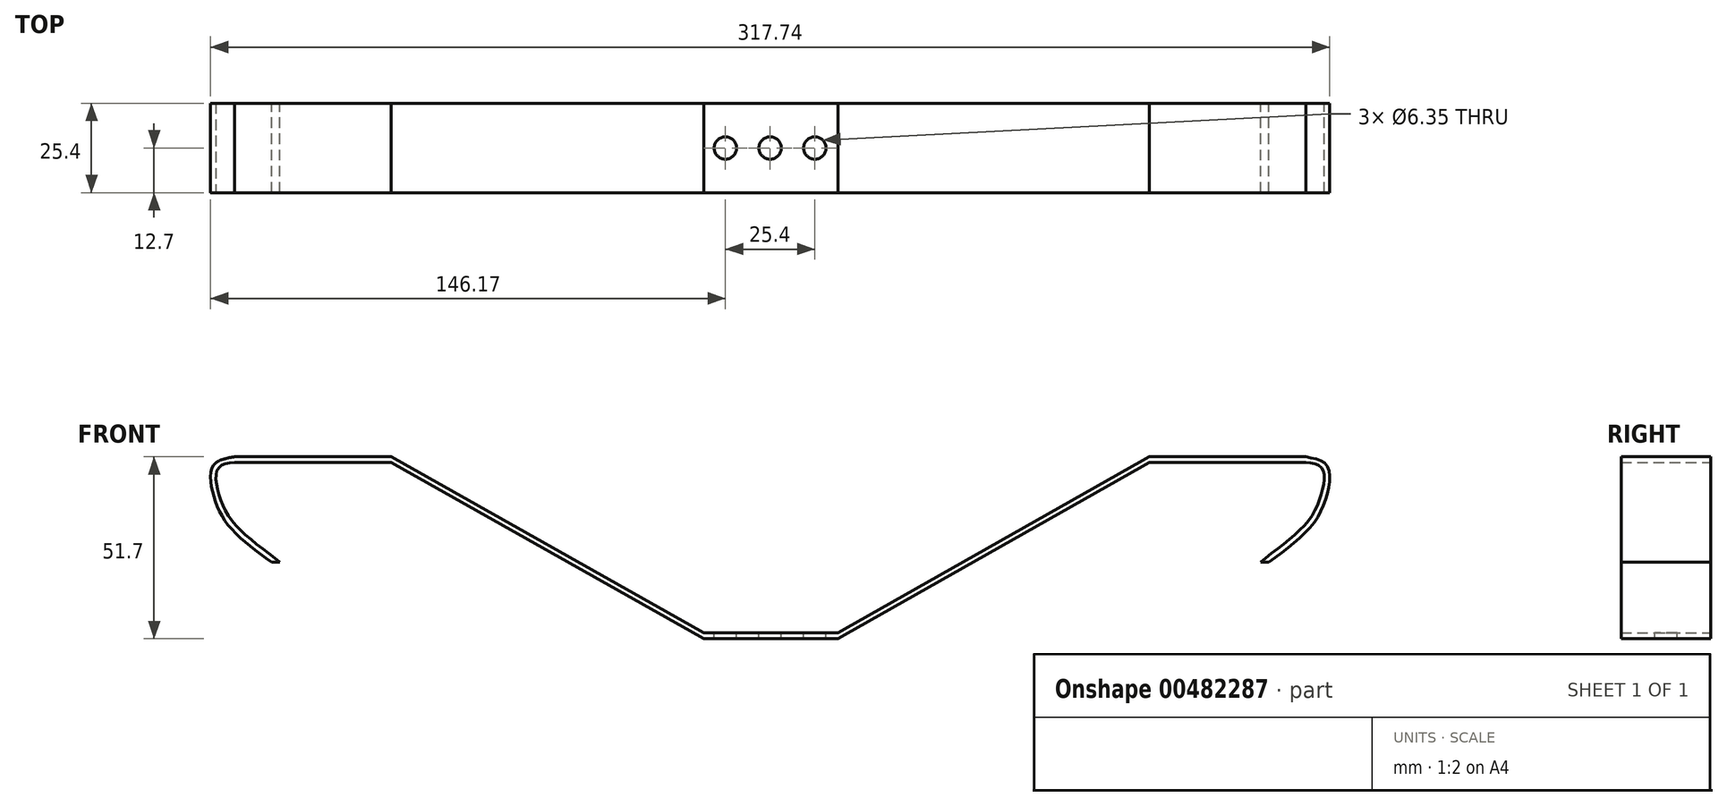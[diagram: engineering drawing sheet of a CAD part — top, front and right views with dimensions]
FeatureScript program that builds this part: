
annotation { "Feature Type Name" : "Feature", "Feature Type Description" : "" }
export const myFeature = defineFeature(function(context is Context, id is Id, definition is map)
    precondition{}
    {
        {
            var Q0;
            Q0=qCreatedBy(makeId("Front.planeOp"),FACE);
            var sketch = newSketch(context, id + "F0", { "sketchPlane" : qUnion([Q0])});
            skLineSegment(sketch, "E0.top", {"start": v(19.25, -0.9) * mm, "end": v(-18.85, -0.9) * mm});
            skPoint(sketch, "E0.middle", {"position": v(0, 0) * mm});
            skLineSegment(sketch, "E1", {"start": v(-18.85, -0.9) * mm, "end": v(-107.65, 49.21) * mm});
            skLineSegment(sketch, "E2", {"start": v(-107.65, 50.8) * mm, "end": v(-152.1, 50.8) * mm});
            skLineSegment(sketch, "E3", {"start": v(-107.65, 49.21) * mm, "end": v(-152.1, 49.21) * mm});
            skLineSegment(sketch, "E4", {"start": v(107.65, 50.8) * mm, "end": v(152.1, 50.8) * mm});
            skLineSegment(sketch, "E5", {"start": v(-152.1, 50.8) * mm, "end": v(-152.1, 49.21) * mm});
            skLineSegment(sketch, "E6", {"start": v(19.25, -0.9) * mm, "end": v(107.66, 49.15) * mm});
            skLineSegment(sketch, "E7", {"start": v(107.66, 49.15) * mm, "end": v(152.1, 49.21) * mm});
            skLineSegment(sketch, "E8", {"start": v(107.65, 50.8) * mm, "end": v(19.25, 0.75) * mm});
            skLineSegment(sketch, "E9", {"start": v(19.25, 0.75) * mm, "end": v(-18.85, 0.75) * mm});
            skLineSegment(sketch, "E10", {"start": v(-18.85, 0.75) * mm, "end": v(-107.65, 50.8) * mm});
            skFitSpline(sketch, "E11", {"points": [v(-152.1, 49.21) * mm, v(-156.77, 47.43) * mm, v(-156.79, 41.3) * mm, v(-152.51, 32.25) * mm, v(-140.68, 21.96) * mm], "startDerivative": vector(-31.73, -0.85) * mm, "endDerivative": vector(39.6, -32.24) * mm});
            skFitSpline(sketch, "E12", {"points": [v(-152.1, 50.8) * mm, v(-157.94, 48.5) * mm, v(-158.31, 40.86) * mm, v(-153.66, 31.16) * mm, v(-141.57, 20.81) * mm], "startDerivative": vector(-33.14, -6.46) * mm, "endDerivative": vector(42.23, -31.67) * mm});
            skLineSegment(sketch, "E13", {"start": v(-140.68, 21.96) * mm, "end": v(-139.27, 20.81) * mm});
            skLineSegment(sketch, "E14", {"start": v(-139.27, 20.81) * mm, "end": v(-141.57, 20.81) * mm});
            skLineSegment(sketch, "E15.MirrorCS", {"start": v(140.68, 21.96) * mm, "end": v(139.27, 20.81) * mm});
            skLineSegment(sketch, "E16.MirrorCS", {"start": v(139.27, 20.81) * mm, "end": v(141.57, 20.81) * mm});
            skFitSpline(sketch, "E17.MirrorCS", {"points": [v(152.1, 49.21) * mm, v(156.77, 47.43) * mm, v(156.79, 41.3) * mm, v(152.51, 32.25) * mm, v(140.68, 21.96) * mm], "startDerivative": vector(31.73, -0.85) * mm, "endDerivative": vector(-39.6, -32.24) * mm});
            skFitSpline(sketch, "E18.MirrorCS", {"points": [v(152.1, 50.8) * mm, v(157.94, 48.5) * mm, v(158.31, 40.86) * mm, v(153.66, 31.16) * mm, v(141.57, 20.81) * mm], "startDerivative": vector(33.14, -6.46) * mm, "endDerivative": vector(-42.23, -31.67) * mm});
            skLineSegment(sketch, "E19", {"start": v(-152.1, 49.21) * mm, "end": v(-164.8, 49.16) * mm});
            skSolve(sketch);
        }
        {
            var Q0;
            Q0 = qSketchRegion(id + "F0", true);
            extrude(context, id + "F1", {"entities" : qUnion([Q0]), "depth" : 25.4 * mm});
        }
        {
            var Q0;
            Q0=makeQuery(id+"F1.opExtrude","SWEPT_FACE",FACE,{"disambiguationData":[OSD([sQuery(id+"F0.wireOp",EDGE,"E9")])]});
            var sketch = newSketch(context, id + "F2", { "sketchPlane" : qUnion([Q0])});
            skCircle(sketch, "E20", {"center": v(0, -12.7) * mm, "radius": 3.18 * mm});
            skCircle(sketch, "E21", {"center": v(-12.7, -12.7) * mm, "radius": 3.18 * mm});
            skCircle(sketch, "E22", {"center": v(12.7, -12.7) * mm, "radius": 3.18 * mm});
            skSolve(sketch);
        }
        {
            var Q0;
            Q0 = qSketchRegion(id + "F2", true);
            extrude(context, id + "F3", {"entities" : qUnion([Q0]), "operationType" : NewBodyOperationType.REMOVE, "endBound" : BoundingType.SYMMETRIC, "oppositeDirection" : true, "depth" : 25.4 * mm});
        }
    });
